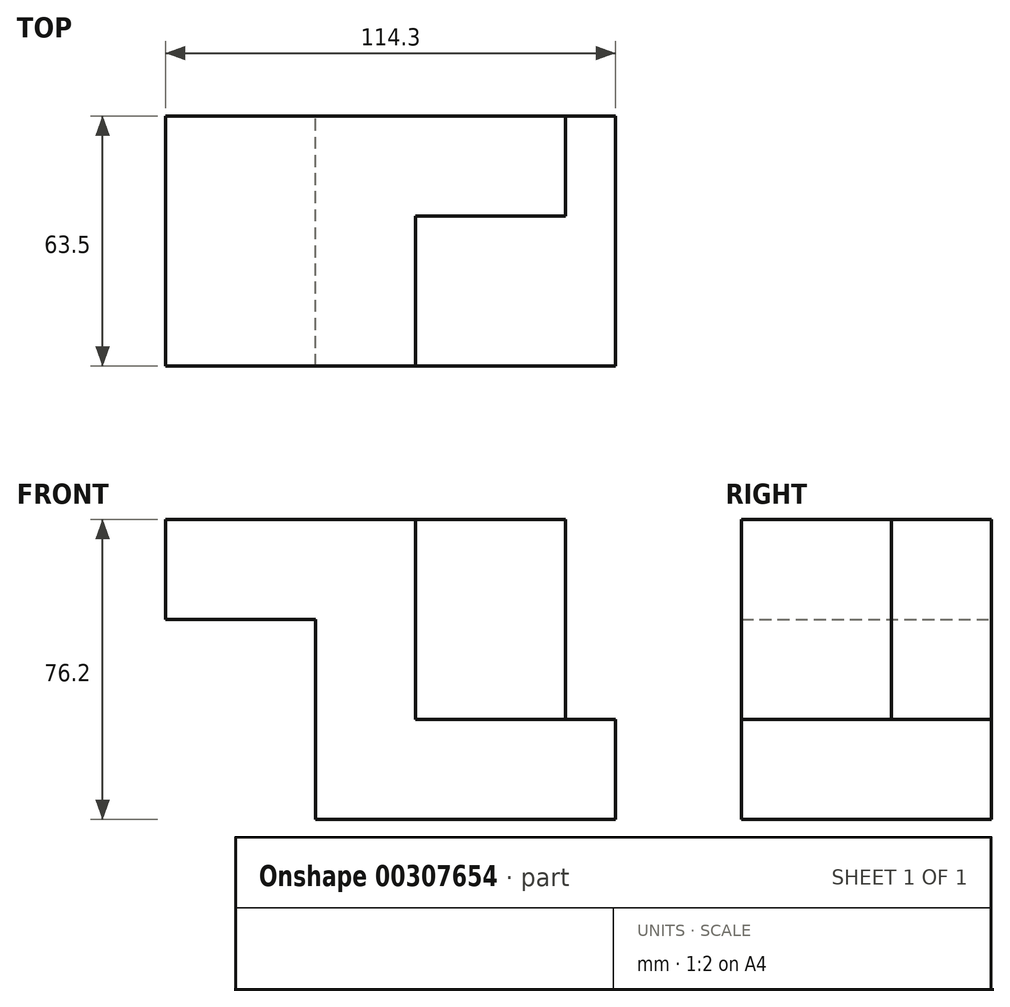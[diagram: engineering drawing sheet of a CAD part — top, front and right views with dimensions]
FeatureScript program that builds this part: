
annotation { "Feature Type Name" : "Feature", "Feature Type Description" : "" }
export const myFeature = defineFeature(function(context is Context, id is Id, definition is map)
    precondition{}
    {
        {
            var Q0;
            Q0=qCreatedBy(makeId("Front.planeOp"),FACE);
            var sketch = newSketch(context, id + "F0", { "sketchPlane" : qUnion([Q0])});
            skLineSegment(sketch, "E0", {"start": v(-68.7, 59.76) * mm, "end": v(-5.2, 59.76) * mm});
            skLineSegment(sketch, "E1", {"start": v(-5.2, 59.76) * mm, "end": v(-5.2, 8.96) * mm});
            skLineSegment(sketch, "E2", {"start": v(-5.2, 8.96) * mm, "end": v(45.6, 8.96) * mm});
            skLineSegment(sketch, "E3", {"start": v(45.6, 8.96) * mm, "end": v(45.6, -16.44) * mm});
            skLineSegment(sketch, "E4", {"start": v(45.6, -16.44) * mm, "end": v(-30.6, -16.44) * mm});
            skLineSegment(sketch, "E5", {"start": v(-30.6, -16.44) * mm, "end": v(-30.6, 34.36) * mm});
            skLineSegment(sketch, "E6", {"start": v(-30.6, 34.36) * mm, "end": v(-68.7, 34.36) * mm});
            skLineSegment(sketch, "E7", {"start": v(-68.7, 34.36) * mm, "end": v(-68.7, 59.76) * mm});
            skSolve(sketch);
        }
        {
            var Q0;
            Q0=makeQuery(id+"F0.imprint","IMPRINT",FACE,{"disambiguationData":[TD([[makeQuery(id+"F0.imprint","IMPRINT",EDGE,{"derivedFrom":sQuery(id+"F0.wireOp",EDGE,"E0")}),-1.0]])]});
            extrude(context, id + "F1", {"entities" : qUnion([Q0]), "depth" : 63.5 * mm});
        }
        {
            var Q0;
            Q0=makeQuery(id+"F1.opExtrude","CAP_FACE",FACE,{"disambiguationData":[OSD([sQuery(id+"F0.wireOp",EDGE,"E0"),sQuery(id+"F0.wireOp",EDGE,"E1"),sQuery(id+"F0.wireOp",EDGE,"E2"),sQuery(id+"F0.wireOp",EDGE,"E3"),sQuery(id+"F0.wireOp",EDGE,"E4"),sQuery(id+"F0.wireOp",EDGE,"E5"),sQuery(id+"F0.wireOp",EDGE,"E6"),sQuery(id+"F0.wireOp",EDGE,"E7")])],"isStart":true});
            var sketch = newSketch(context, id + "F2", { "sketchPlane" : qUnion([Q0])});
            skLineSegment(sketch, "E8", {"start": v(5.2, 59.76) * mm, "end": v(-32.9, 59.76) * mm});
            skLineSegment(sketch, "E9", {"start": v(-32.9, 59.76) * mm, "end": v(-32.9, 8.96) * mm});
            skLineSegment(sketch, "E10", {"start": v(-32.9, 8.96) * mm, "end": v(5.2, 8.96) * mm});
            skLineSegment(sketch, "E11", {"start": v(5.2, 8.96) * mm, "end": v(5.2, 59.76) * mm});
            skSolve(sketch);
        }
        {
            var Q0;
            Q0 = qSketchRegion(id + "F2", true);
            extrude(context, id + "F3", {"entities" : qUnion([Q0]), "operationType" : NewBodyOperationType.ADD, "depth" : -25.4 * mm});
        }
    });
